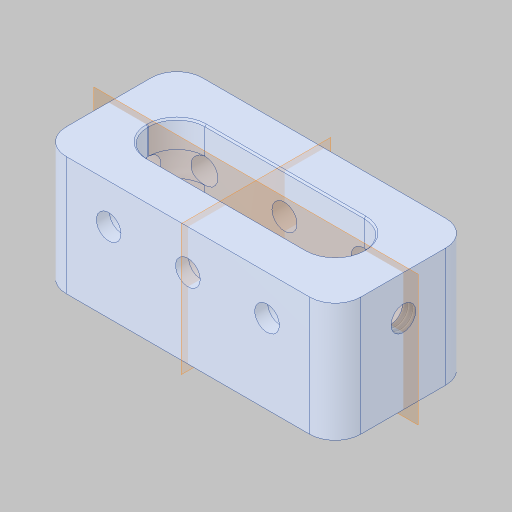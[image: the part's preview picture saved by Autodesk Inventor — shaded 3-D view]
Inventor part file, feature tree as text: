
AUTODESK INVENTOR PART (.ipt)
format: ipt  version: 2023.5 (Build 275446000, 446)  size: 354,304 bytes
history: native  units: in
note: dims shown in document units (in); Inventor stores cm internally (conversion verified against a paired STEP export)
features: sketch x4, hole x3, projected_geometry x3, extrude x2, chamfer x1
ambient origin geometry x8: Origin, YZ Plane, XZ Plane, XY Plane, X Axis, Y Axis, Z Axis, Center Point
bodies: Solid1 (feature_tree)
feature tree (13):
  extrude  "Extrusion1"  Depth=1.0in TaperAngle=0.0deg
  hole  "Hole1"  [1 undecoded]
  hole  "Hole3"  [1 undecoded]
  sketch  "Sketch5"  dims[d26=0.156in d27=0.38in d28=0.375in d29=0.25in d30=0.5635in d31=1.0in d32=0.8108in d33=0.0625in d34=0.75in d35=0.375in]
  extrude  "Extrusion2"  Depth=0.375in
  hole  "Hole4"  [1 undecoded]
  sketch  "Sketch1"  dims[d0=0.0625in d1=1.0in d2=0.0in]
  projected_geometry  "Projected Loop1"
  sketch  "Sketch2"  dims[d3=0.156in d4=0.38in d5=0.385in d6=0.25in d7=0.563in d8=1.0in d9=0.8108in]
  projected_geometry  "Projected Loop2"
  sketch  "Sketch4"  dims[d17=0.156in d18=0.38in d19=0.385in d20=0.25in d21=0.563in d22=1.0in d23=0.8108in d24=1.0in d25=0.0in]
  chamfer  "Chamfer2"  [1 undecoded]
  projected_geometry  "Project Cut Edges1"
note: 4 required parameter values undecoded (feature->parameter linkage not recoverable at this tier; creation-order binding heuristic only, values carry confidence <= 0.55)
